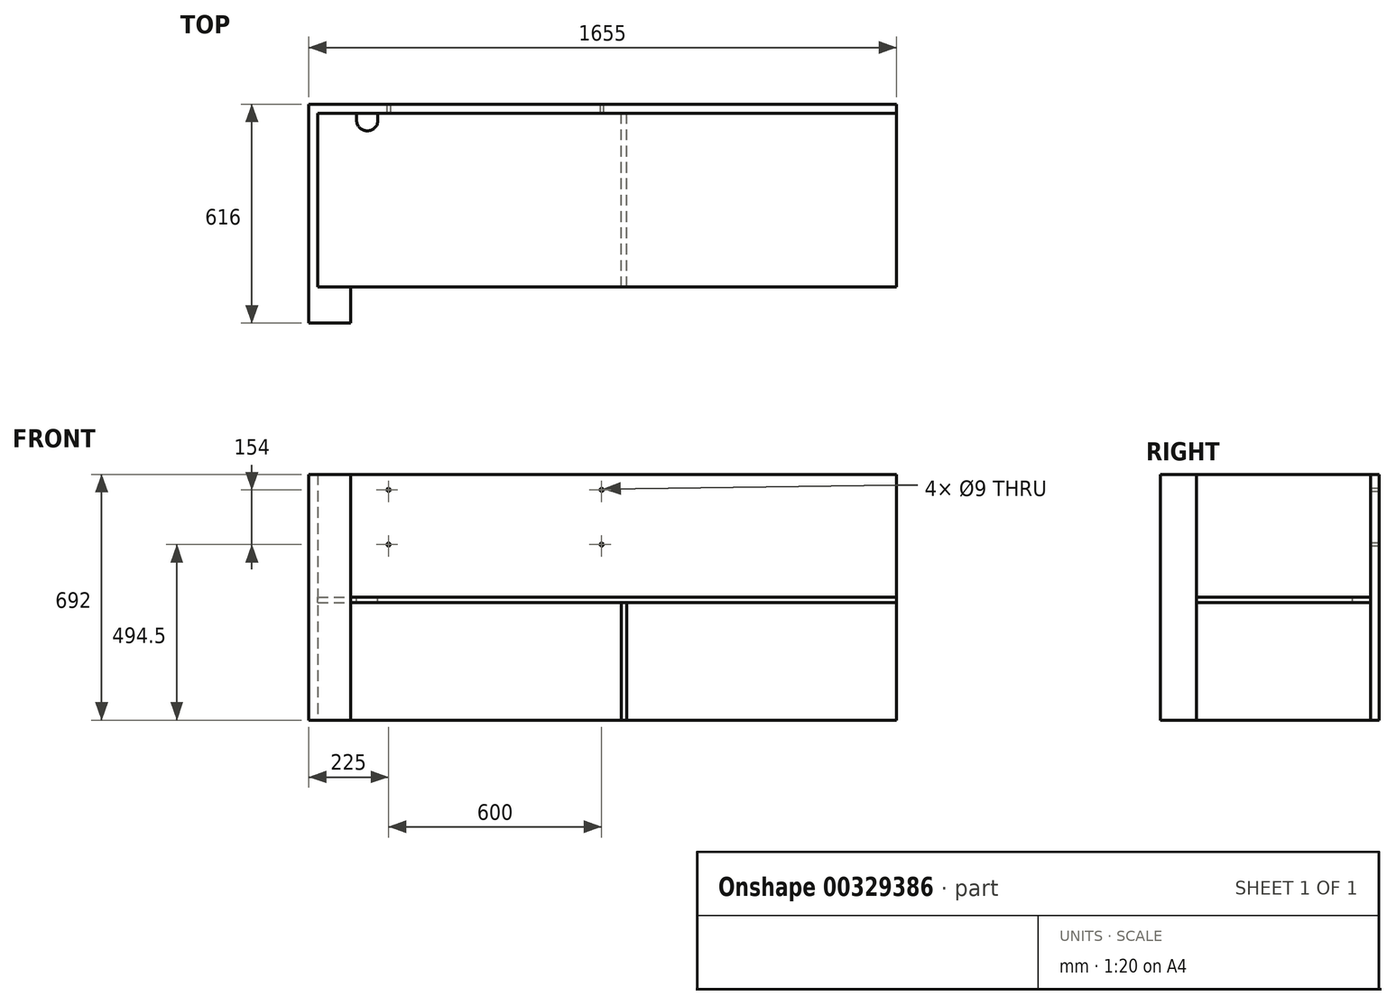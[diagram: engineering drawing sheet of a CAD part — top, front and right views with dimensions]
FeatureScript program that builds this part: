
annotation { "Feature Type Name" : "Feature", "Feature Type Description" : "" }
export const myFeature = defineFeature(function(context is Context, id is Id, definition is map)
    precondition{}
    {
        {
            var Q0;
            Q0=qCreatedBy(makeId("Top.planeOp"),FACE);
            var sketch = newSketch(context, id + "F0", { "sketchPlane" : qUnion([Q0])});
            skLineSegment(sketch, "E0.bottom", {"start": v(-815, 245) * mm, "end": v(-705, 245) * mm});
            skLineSegment(sketch, "E0.top", {"start": v(-815, -245) * mm, "end": v(815, -245) * mm});
            skLineSegment(sketch, "E0.left", {"start": v(-815, 245) * mm, "end": v(-815, -245) * mm});
            skLineSegment(sketch, "E0.right", {"start": v(815, 245) * mm, "end": v(815, -245) * mm});
            skLineSegment(sketch, "E1", {"start": v(-645, 245) * mm, "end": v(815, 245) * mm});
            skLineSegment(sketch, "E2", {"start": v(-705, 245) * mm, "end": v(-705, 225) * mm});
            skLineSegment(sketch, "E3", {"start": v(-645, 245) * mm, "end": v(-645, 225) * mm});
            skArc(sketch, "E4", {"start": v(-705, 225) * mm, "mid": v(-675, 195) * mm, "end": v(-645, 225) * mm});
            skLineSegment(sketch, "E5", {"start": v(-815, -245) * mm, "end": v(815, 245) * mm, "construction": true});
            skSolve(sketch);
        }
        {
            var Q0;
            Q0=makeQuery(id+"F0.imprint","IMPRINT",FACE,{"disambiguationData":[TD([[makeQuery(id+"F0.imprint","IMPRINT",EDGE,{"derivedFrom":sQuery(id+"F0.wireOp",EDGE,"E0.bottom")}),-1.0]])]});
            extrude(context, id + "F1", {"entities" : qUnion([Q0]), "oppositeDirection" : true, "depth" : 15 * mm});
        }
        {
            var Q0;
            Q0=makeQuery(id+"F1.opExtrude","CAP_FACE",FACE,{"disambiguationData":[OSD([sQuery(id+"F0.wireOp",EDGE,"E0.bottom"),sQuery(id+"F0.wireOp",EDGE,"E0.top"),sQuery(id+"F0.wireOp",EDGE,"E0.left"),sQuery(id+"F0.wireOp",EDGE,"E0.right"),sQuery(id+"F0.wireOp",EDGE,"E1"),sQuery(id+"F0.wireOp",EDGE,"E2"),sQuery(id+"F0.wireOp",EDGE,"E3"),sQuery(id+"F0.wireOp",EDGE,"E4")])],"isStart":true});
            var sketch = newSketch(context, id + "F2", { "sketchPlane" : qUnion([Q0])});
            skLineSegment(sketch, "E6", {"start": v(-815, -245) * mm, "end": v(-815, 245) * mm});
            skLineSegment(sketch, "E7", {"start": v(-815, 245) * mm, "end": v(815, 245) * mm});
            skLineSegment(sketch, "E8", {"start": v(815, 245) * mm, "end": v(815, 270) * mm});
            skLineSegment(sketch, "E9", {"start": v(815, 270) * mm, "end": v(-840, 270) * mm});
            skLineSegment(sketch, "E10", {"start": v(-840, 270) * mm, "end": v(-840, -346) * mm});
            skLineSegment(sketch, "E11", {"start": v(-840, -346) * mm, "end": v(-722, -346) * mm});
            skLineSegment(sketch, "E12", {"start": v(-722, -346) * mm, "end": v(-722, -245) * mm});
            skLineSegment(sketch, "E13", {"start": v(-722, -245) * mm, "end": v(-815, -245) * mm});
            skSolve(sketch);
        }
        {
            var Q0;
            {var subQ4=sQuery(id+"F2.wireOp",EDGE,"E6");Q0=makeQuery(id+"F2.imprint","IMPRINT",FACE,{"disambiguationData":[TD([[makeQuery(id+"F2.imprint","IMPRINT",EDGE,{"derivedFrom":subQ4}),-1.0]])]});}
            extrude(context, id + "F3", {"entities" : qUnion([Q0]), "endBound" : BoundingType.SYMMETRIC, "depth" : 2 * 346 * mm});
        }
        {
            var Q0;
            Q0=makeQuery(id+"F1.opExtrude","CAP_FACE",FACE,{"disambiguationData":[OSD([sQuery(id+"F0.wireOp",EDGE,"E0.bottom"),sQuery(id+"F0.wireOp",EDGE,"E0.top"),sQuery(id+"F0.wireOp",EDGE,"E0.left"),sQuery(id+"F0.wireOp",EDGE,"E0.right"),sQuery(id+"F0.wireOp",EDGE,"E1"),sQuery(id+"F0.wireOp",EDGE,"E2"),sQuery(id+"F0.wireOp",EDGE,"E3"),sQuery(id+"F0.wireOp",EDGE,"E4")])],"isStart":false});
            var sketch = newSketch(context, id + "F4", { "sketchPlane" : qUnion([Q0])});
            skLineSegment(sketch, "E14.bottom", {"start": v(55, 245) * mm, "end": v(40, 245) * mm});
            skLineSegment(sketch, "E14.top", {"start": v(55, -245) * mm, "end": v(40, -245) * mm});
            skLineSegment(sketch, "E14.left", {"start": v(55, 245) * mm, "end": v(55, -245) * mm});
            skLineSegment(sketch, "E14.right", {"start": v(40, 245) * mm, "end": v(40, -245) * mm});
            skSolve(sketch);
        }
        {
            var Q0;
            Q0=makeQuery(id+"F4.imprint","IMPRINT",FACE,{"disambiguationData":[TD([[makeQuery(id+"F4.imprint","IMPRINT",EDGE,{"derivedFrom":sQuery(id+"F4.wireOp",EDGE,"E14.bottom")}),-1.0]])]});
            extrude(context, id + "F5", {"entities" : qUnion([Q0]), "depth" : 331 * mm});
        }
        {
            var Q0;
            Q0=makeQuery(id+"F3.opExtrude","SWEPT_FACE",FACE,{"disambiguationData":[OSD([sQuery(id+"F2.wireOp",EDGE,"E7")])]});
            var sketch = newSketch(context, id + "F6", { "sketchPlane" : qUnion([Q0])});
            skLineSegment(sketch, "E15", {"start": v(-615, 346) * mm, "end": v(-615, -346) * mm, "construction": true});
            skLineSegment(sketch, "E16", {"start": v(-15, 346) * mm, "end": v(-15, -346) * mm, "construction": true});
            skLineSegment(sketch, "E17", {"start": v(-815, 331) * mm, "end": v(815, 331) * mm, "construction": true});
            skLineSegment(sketch, "E18", {"start": v(-815, 302.5) * mm, "end": v(815, 302.5) * mm, "construction": true});
            skLineSegment(sketch, "E19", {"start": v(-815, 252.5) * mm, "end": v(815, 252.5) * mm, "construction": true});
            skLineSegment(sketch, "E20", {"start": v(-815, 148.5) * mm, "end": v(815, 148.5) * mm, "construction": true});
            skCircle(sketch, "E21", {"center": v(-615, 302.5) * mm, "radius": 4.5 * mm});
            skCircle(sketch, "E22", {"center": v(-615, 148.5) * mm, "radius": 4.5 * mm});
            skCircle(sketch, "E23", {"center": v(-15, 302.5) * mm, "radius": 4.5 * mm});
            skCircle(sketch, "E24", {"center": v(-15, 148.5) * mm, "radius": 4.5 * mm});
            skLineSegment(sketch, "E25.bottom", {"start": v(-455, 235) * mm, "end": v(-185, 235) * mm, "construction": true});
            skLineSegment(sketch, "E25.top", {"start": v(-455, 25) * mm, "end": v(-185, 25) * mm, "construction": true});
            skLineSegment(sketch, "E25.left", {"start": v(-455, 235) * mm, "end": v(-455, 25) * mm, "construction": true});
            skLineSegment(sketch, "E25.right", {"start": v(-185, 235) * mm, "end": v(-185, 25) * mm, "construction": true});
            skLineSegment(sketch, "E26", {"start": v(-455, 25) * mm, "end": v(-185, 235) * mm, "construction": true});
            skPoint(sketch, "E27", {"position": v(-320, 130) * mm});
            skSolve(sketch);
        }
        {
            var Q0;
            Q0 = qSketchRegion(id + "F6", true);
            extrude(context, id + "F7", {"entities" : qUnion([Q0]), "operationType" : NewBodyOperationType.REMOVE, "oppositeDirection" : true, "depth" : 25 * mm});
        }
    });
